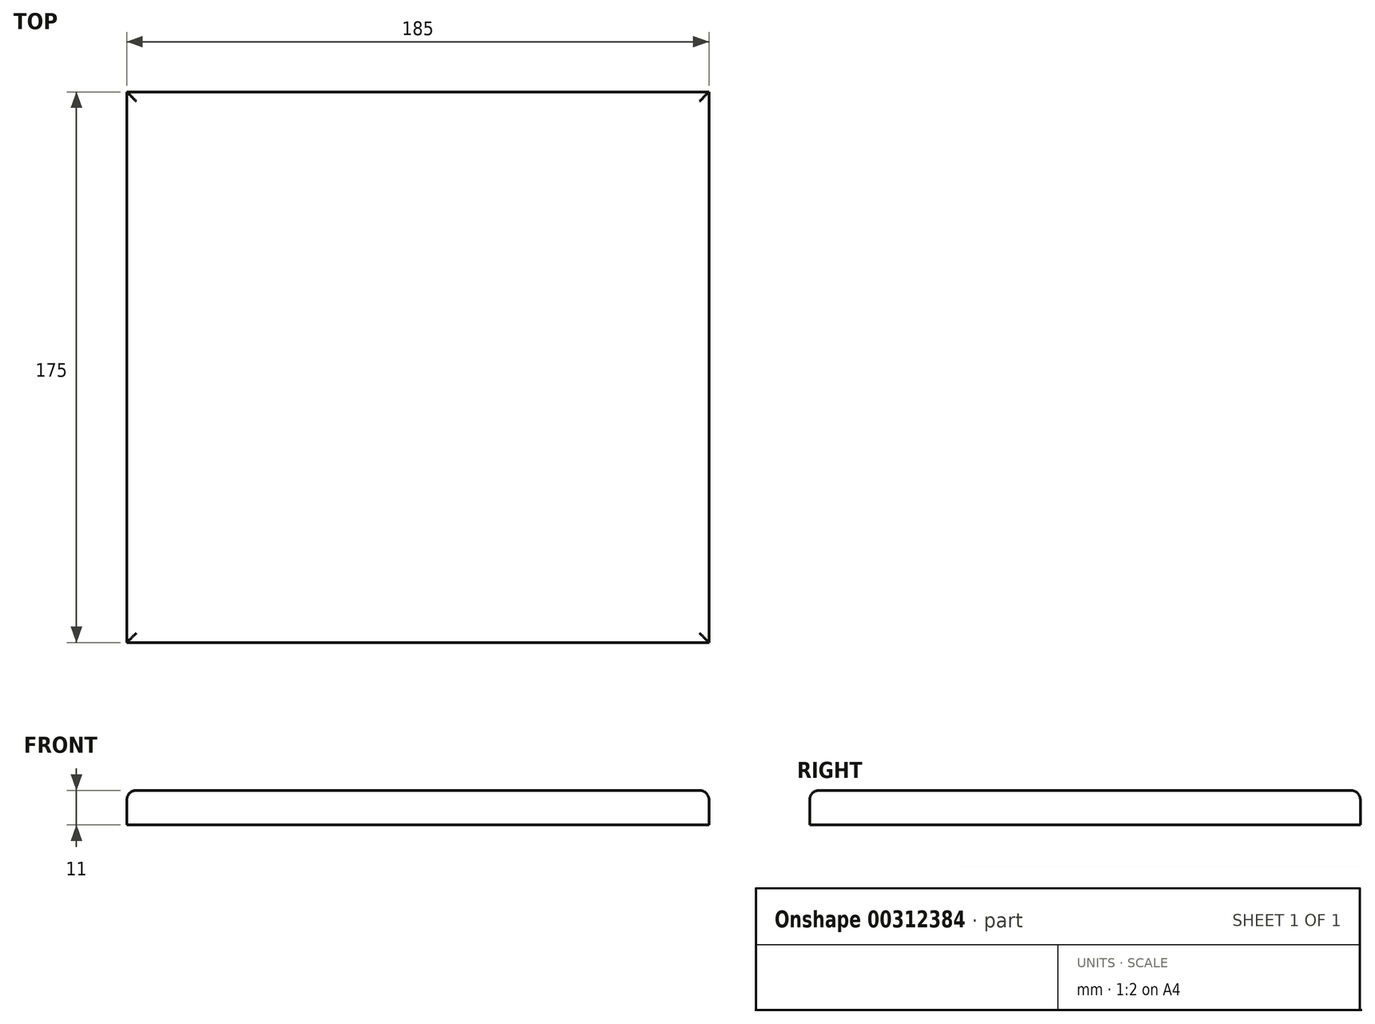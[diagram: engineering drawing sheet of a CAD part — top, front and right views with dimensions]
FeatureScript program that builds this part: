
annotation { "Feature Type Name" : "Feature", "Feature Type Description" : "" }
export const myFeature = defineFeature(function(context is Context, id is Id, definition is map)
    precondition{}
    {
        {
            var Q0;
            Q0=qCreatedBy(makeId("Top.planeOp"),FACE);
            var sketch = newSketch(context, id + "F0", { "sketchPlane" : qUnion([Q0])});
            skLineSegment(sketch, "E0.bottom", {"start": v(92.5, -87.5) * mm, "end": v(-92.5, -87.5) * mm});
            skLineSegment(sketch, "E0.top", {"start": v(92.5, 87.5) * mm, "end": v(-92.5, 87.5) * mm});
            skLineSegment(sketch, "E0.left", {"start": v(92.5, -87.5) * mm, "end": v(92.5, 87.5) * mm});
            skLineSegment(sketch, "E0.right", {"start": v(-92.5, -87.5) * mm, "end": v(-92.5, 87.5) * mm});
            skPoint(sketch, "E0.middle", {"position": v(0, 0) * mm});
            skSolve(sketch);
        }
        {
            var Q0;
            Q0 = qSketchRegion(id + "F0", true);
            extrude(context, id + "F1", {"entities" : qUnion([Q0]), "depth" : 11 * mm});
        }
        {
            var Q0;
            Q0=makeQuery(id+"F1.opExtrude","CAP_EDGE",EDGE,{"disambiguationData":[OSD([sQuery(id+"F0.wireOp",EDGE,"E0.bottom")])],"isStart":false});
            var Q1;
            Q1=makeQuery(id+"F1.opExtrude","CAP_EDGE",EDGE,{"disambiguationData":[OSD([sQuery(id+"F0.wireOp",EDGE,"E0.right")])],"isStart":false});
            var Q2;
            Q2=makeQuery(id+"F1.opExtrude","CAP_EDGE",EDGE,{"disambiguationData":[OSD([sQuery(id+"F0.wireOp",EDGE,"E0.top")])],"isStart":false});
            var Q3;
            Q3=makeQuery(id+"F1.opExtrude","CAP_EDGE",EDGE,{"disambiguationData":[OSD([sQuery(id+"F0.wireOp",EDGE,"E0.left")])],"isStart":false});
            fillet(context, id + "F2", {"entities" : qUnion([Q0, Q1, Q2, Q3]), "radius" : 3 * mm, "tangentPropagation" : true, "allowEdgeOverflow" : false});
        }
    });
